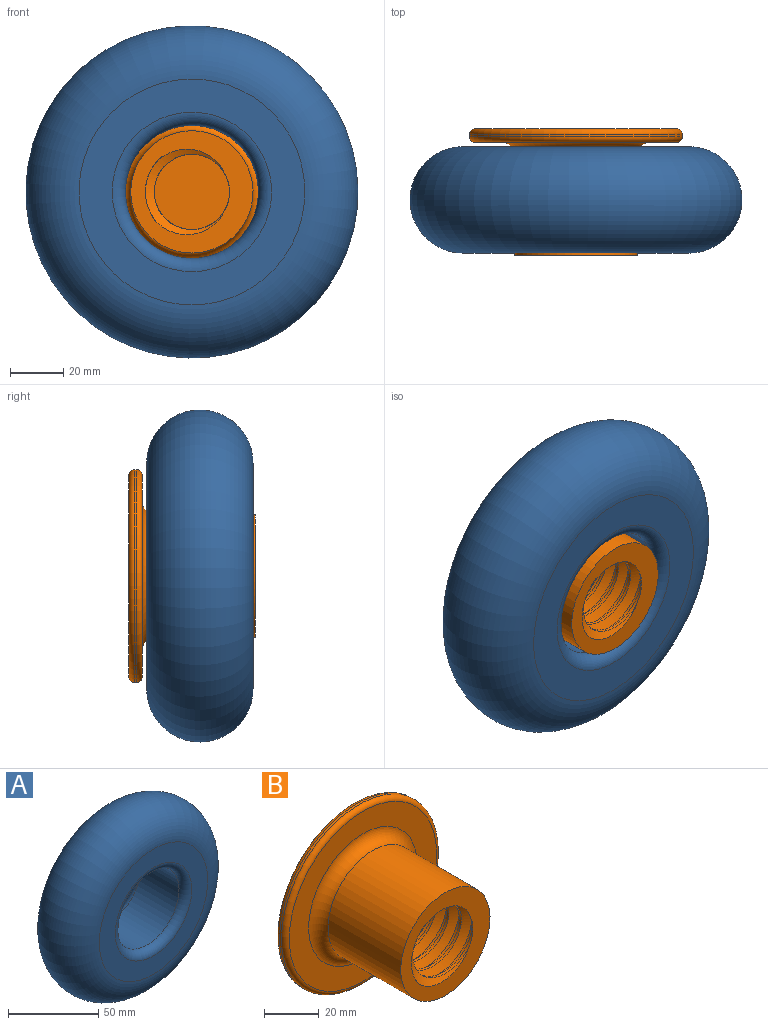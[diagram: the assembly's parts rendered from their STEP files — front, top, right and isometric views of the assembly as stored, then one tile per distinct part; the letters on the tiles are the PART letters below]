
ASSEMBLY  parts=2 mates=1
PART A: 6 faces, bbox 135.3x40x135.3 mm
  f0: cylinder r=25mm len=50mm, axis (0,1,0), area 4712.4mm2, adj f4,f5
  f1: plane 85x85mm, normal (0,-1,0), area 2847.1mm2, adj f3,f5
  f2: plane 85x85mm, normal (0,1,0), area 2847.1mm2, adj f3,f4
  f3: torus R=42.5mm, axis (0,-1,0), area 21804.9mm2, adj f1,f2
  f4: torus R=30mm, axis (0,-1,0), area 1323.4mm2, adj f0,f2
  f5: torus R=30mm, axis (0,-1,0), area 1323.4mm2, adj f0,f1
PART B: 24 faces, bbox 88.2x51.8x88.2 mm
  f0: bspline ~35x33.84mm, area 1823.3mm2, adj f1,f4,f8,f9
  f1: bspline ~33.65x32.72mm, area 510.3mm2, adj f0,f3,f5,f6,f7,f8
  f2: bspline ~35.09x20.35mm, area 92.9mm2, adj f3,f6,f8,f9
  f3: bspline ~12.32x7.13mm, area 2.3mm2, adj f1,f2,f8
  f4: bspline ~35.09x20.35mm, area 92.9mm2, adj f0,f5,f7,f9
  f5: bspline ~12.32x7.13mm, area 2.3mm2, adj f1,f4,f7
  f6: bspline ~40.41x35.17mm, area 1821.9mm2, adj f1,f2,f7,f9
  f7: plane 47.63x47.63mm, normal (0,-1,0), area 860.3mm2, adj f1,f4,f5,f6,f9,f10
  f8: plane 33.81x33.3mm, normal (0,-1,0), area 801.6mm2, adj f0,f1,f2,f3,f9
  f9: cylinder r=17.5mm len=35mm, axis (0,-1,0), area 636.1mm2, adj f0,f2,f4,f6,f7,f8
  f10: cylinder r=23mm len=46mm, axis (0,-1,0), area 5419.2mm2, adj f7,f11
  f11: torus R=28mm, axis (0,-1,0), area 1224.7mm2, adj f10,f12
  f12: plane 76x76mm, normal (0,-1,0), area 2073.5mm2, adj f11,f13
  f13: torus R=38mm, axis (0,-1,0), area 775.2mm2, adj f12,f14
  f14: cylinder r=40mm len=80mm, axis (0,-1,0), area 251.3mm2, adj f13,f15
  f15: torus R=38mm, axis (0,-1,0), area 775.2mm2, adj f14,f16
  f16: plane 76x76mm, normal (0,1,0), area 4471.5mm2, adj f15,f17,f18,f19,f20,f21,f22
  f17: plane 7.5x4.4mm, normal (-0.88,0,-0.47), area 37.5mm2, adj f16,f18,f22,f23
  f18: plane 7.5x4.25mm, normal (-0.85,0,0.53), area 37.5mm2, adj f16,f17,f19,f23
  f19: plane 7.5x5mm, normal (0.03,0,1), area 37.5mm2, adj f16,f18,f20,f23
  f20: plane 7.5x4.4mm, normal (0.88,0,0.47), area 37.5mm2, adj f16,f19,f21,f23
  f21: plane 7.5x4.25mm, normal (0.85,0,-0.53), area 37.5mm2, adj f16,f20,f22,f23
  f22: plane 7.5x5mm, normal (-0.03,0,-1), area 37.5mm2, adj f16,f17,f21,f23
  f23: plane 10x8.81mm, normal (0,1,0), area 65mm2, adj f17,f18,f19,f20,f21,f22
PLACE A rot(axis=(0,-1,0),41.3deg) t=(0,25.78,0)mm
PLACE B at identity fixed
MATE cylindrical B.f10 <-> A.f0  axis (0,-1,0) through (0,23.75,0)mm
